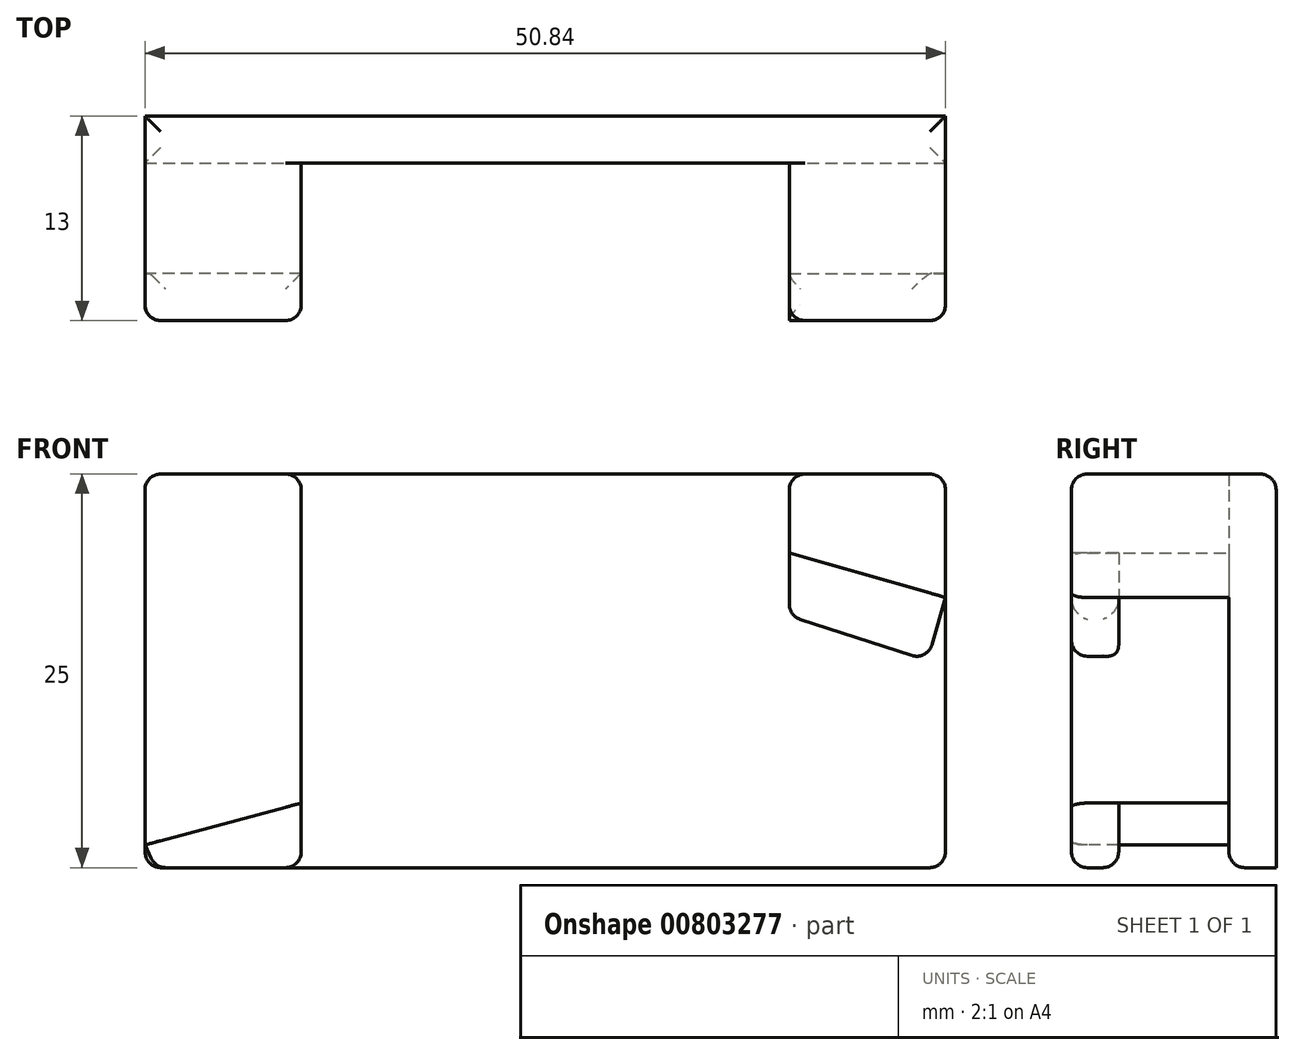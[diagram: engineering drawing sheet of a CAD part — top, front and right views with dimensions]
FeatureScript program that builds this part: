
annotation { "Feature Type Name" : "Feature", "Feature Type Description" : "" }
export const myFeature = defineFeature(function(context is Context, id is Id, definition is map)
    precondition{}
    {
        {
            var Q0;
            Q0=qCreatedBy(makeId("Top.planeOp"),FACE);
            var sketch = newSketch(context, id + "F0", { "sketchPlane" : qUnion([Q0])});
            skPoint(sketch, "E0.rect.middle", {"position": v(0, 0) * mm});
            skLineSegment(sketch, "E1", {"start": v(13.42, 12.71) * mm, "end": v(13.42, 8.71) * mm});
            skLineSegment(sketch, "E2", {"start": v(13.42, 8.7) * mm, "end": v(37.42, 8.71) * mm});
            skLineSegment(sketch, "E3", {"start": v(37.42, 8.71) * mm, "end": v(37.42, 12.71) * mm});
            skLineSegment(sketch, "E4", {"start": v(37.42, 12.71) * mm, "end": v(50.84, 12.71) * mm});
            skLineSegment(sketch, "E5", {"start": v(13.42, 12.71) * mm, "end": v(0, 12.71) * mm});
            skLineSegment(sketch, "E6", {"start": v(0, 0) * mm, "end": v(50.84, 0) * mm});
            skLineSegment(sketch, "E7", {"start": v(0, 12.71) * mm, "end": v(0, 0) * mm});
            skLineSegment(sketch, "E8", {"start": v(50.84, 12.71) * mm, "end": v(50.84, 0) * mm});
            skSolve(sketch);
        }
        {
            var Q0;
            Q0=makeQuery(id+"F0.imprint","IMPRINT",FACE,{"disambiguationData":[TD([[makeQuery(id+"F0.imprint","IMPRINT",EDGE,{"derivedFrom":sQuery(id+"F0.wireOp",EDGE,"E1")}),-1.0]])]});
            extrude(context, id + "F1", {"entities" : qUnion([Q0]), "depth" : 3 * mm, "offsetDistance" : 25 * mm});
        }
        {
            var Q0;
            Q0=makeQuery(id+"F1.opExtrude","SWEPT_FACE",FACE,{"disambiguationData":[OSD([sQuery(id+"F0.wireOp",EDGE,"E6")])]});
            var sketch = newSketch(context, id + "F2", { "sketchPlane" : qUnion([Q0])});
            skLineSegment(sketch, "E9", {"start": v(50.84, 0) * mm, "end": v(50.84, 25) * mm});
            skLineSegment(sketch, "E10", {"start": v(50.84, 25) * mm, "end": v(0, 25) * mm});
            skLineSegment(sketch, "E11", {"start": v(0, 25) * mm, "end": v(0, 0) * mm});
            skLineSegment(sketch, "E12", {"start": v(0, 0) * mm, "end": v(50.84, 0) * mm});
            skSolve(sketch);
        }
        {
            var Q0;
            Q0=qSketchRegion(id+"F2",true);
            extrude(context, id + "F3", {"entities" : qUnion([Q0]), "operationType" : NewBodyOperationType.ADD, "depth" : 3 * mm});
        }
        {
            var Q0;
            Q0=makeQuery(id+"F3.opExtrude","CAP_FACE",FACE,{"disambiguationData":[OSD([sQuery(id+"F2.wireOp",EDGE,"E9"),sQuery(id+"F2.wireOp",EDGE,"E10"),sQuery(id+"F2.wireOp",EDGE,"E11"),sQuery(id+"F2.wireOp",EDGE,"E12")])],"isStart":false});
            var sketch = newSketch(context, id + "F4", { "sketchPlane" : qUnion([Q0])});
            skLineSegment(sketch, "E13", {"start": v(40.92, 25) * mm, "end": v(40.92, 20) * mm});
            skLineSegment(sketch, "E14", {"start": v(40.92, 20) * mm, "end": v(50.84, 17.16) * mm});
            skLineSegment(sketch, "E15", {"start": v(9.92, 25) * mm, "end": v(9.92, 4.1) * mm});
            skLineSegment(sketch, "E16", {"start": v(9.92, 4.1) * mm, "end": v(0, 1.44) * mm});
            skSolve(sketch);
        }
        {
            var Q0;
            Q0=qSketchRegion(id+"F4",true);
            var Q1;
            {var subQ0=sQuery(id+"F4.wireOp",EDGE,"E15");Q1=makeQuery(id+"F4.imprint","IMPRINT",FACE,{"disambiguationData":[TD([[makeQuery(id+"F4.imprint","IMPRINT",EDGE,{"derivedFrom":subQ0}),-1.0]])]});}
            var Q2;
            {var subQ0=sQuery(id+"F4.wireOp",EDGE,"E13");Q2=makeQuery(id+"F4.imprint","IMPRINT",FACE,{"disambiguationData":[TD([[makeQuery(id+"F4.imprint","IMPRINT",EDGE,{"derivedFrom":subQ0}),1.0]])]});}
            extrude(context, id + "F5", {"entities" : qUnion([Q0, Q1, Q2]), "operationType" : NewBodyOperationType.ADD, "depth" : 10 * mm});
        }
        {
            var Q0;
            Q0=makeQuery(id+"F5.opExtrude","CAP_FACE",FACE,{"disambiguationData":[OSD([sQuery(id+"F2.wireOp",EDGE,"E9"),sQuery(id+"F2.wireOp",EDGE,"E10"),sQuery(id+"F4.wireOp",EDGE,"E13"),sQuery(id+"F4.wireOp",EDGE,"E14")])],"isStart":false});
            var sketch = newSketch(context, id + "F6", { "sketchPlane" : qUnion([Q0])});
            skLineSegment(sketch, "E17", {"start": v(50.84, 17.16) * mm, "end": v(49.7, 13.16) * mm});
            skLineSegment(sketch, "E18", {"start": v(40.92, 20) * mm, "end": v(40.92, 16) * mm});
            skLineSegment(sketch, "E19", {"start": v(40.92, 16) * mm, "end": v(49.7, 13.16) * mm});
            skLineSegment(sketch, "E20", {"start": v(40.92, 16) * mm, "end": v(40.92, 20) * mm});
            skSolve(sketch);
        }
        {
            var Q0;
            Q0=qSketchRegion(id+"F6",true);
            var Q1;
            Q1=makeQuery(id+"F6.imprint","IMPRINT",FACE,{"disambiguationData":[TD([[makeQuery(id+"F6.imprint","IMPRINT",EDGE,{"derivedFrom":sQuery(id+"F6.wireOp",EDGE,"E17")}),-1.0]])]});
            extrude(context, id + "F7", {"entities" : qUnion([Q0, Q1]), "oppositeDirection" : true, "depth" : 3 * mm});
        }
        {
            var Q0;
            Q0=makeQuery(id+"F5.opExtrude","CAP_FACE",FACE,{"disambiguationData":[OSD([sQuery(id+"F2.wireOp",EDGE,"E10"),sQuery(id+"F2.wireOp",EDGE,"E11"),sQuery(id+"F4.wireOp",EDGE,"E15"),sQuery(id+"F4.wireOp",EDGE,"E16")])],"isStart":false});
            var sketch = newSketch(context, id + "F8", { "sketchPlane" : qUnion([Q0])});
            skLineSegment(sketch, "E21", {"start": v(9.92, 4.1) * mm, "end": v(9.92, 0) * mm});
            skLineSegment(sketch, "E22", {"start": v(9.92, 0) * mm, "end": v(0.67, 0) * mm});
            skPoint(sketch, "E22.endSnap0", {"position": v(0.67, 0) * mm});
            skLineSegment(sketch, "E23", {"start": v(0, 1.44) * mm, "end": v(0.67, 0) * mm});
            skSolve(sketch);
        }
        {
            var Q0;
            Q0=qSketchRegion(id+"F8",true);
            var Q1;
            Q1=makeQuery(id+"F8.imprint","IMPRINT",FACE,{"disambiguationData":[TD([[makeQuery(id+"F8.imprint","IMPRINT",EDGE,{"derivedFrom":sQuery(id+"F8.wireOp",EDGE,"E21")}),-1.0]])]});
            extrude(context, id + "F9", {"entities" : qUnion([Q0, Q1]), "oppositeDirection" : true, "depth" : 3 * mm, "offsetDistance" : 25 * mm});
        }
        {
            var Q0;
            Q0=makeQuery(id+"F5.opExtrude","CAP_EDGE",EDGE,{"disambiguationData":[OSD([sQuery(id+"F4.wireOp",EDGE,"E15")])],"isStart":true});
            var Q1;
            Q1=makeQuery(id+"F5.opExtrude","CAP_EDGE",EDGE,{"disambiguationData":[OSD([sQuery(id+"F4.wireOp",EDGE,"E14")])],"isStart":true});
            var Q2;
            Q2=makeQuery(id+"F5.opExtrude","CAP_EDGE",EDGE,{"disambiguationData":[OSD([sQuery(id+"F4.wireOp",EDGE,"E16")])],"isStart":true});
            var Q3;
            Q3=makeQuery(id+"F1.opExtrude","CAP_EDGE",EDGE,{"disambiguationData":[OSD([sQuery(id+"F0.wireOp",EDGE,"E6")])],"isStart":false});
            var Q4;
            Q4=makeQuery(id+"F1.opExtrude","SWEPT_EDGE",EDGE,{"disambiguationData":[OSD([sQuery(id+"F0.wireOp",EDGE,"E1"),sQuery(id+"F0.wireOp",EDGE,"E2")])]});
            fillet(context, id + "F10", {"entities" : qUnion([Q0, Q1, Q2, Q3, Q4]), "radius" : .5 * mm, "tangentPropagation" : true, "allowEdgeOverflow" : false});
        }
        {
            var Q0;
            Q0=makeQuery(id+"F3.boolean.opBoolean","MERGE",FACE,{"derivedFrom":[makeQuery(id+"F1.opExtrude","CAP_FACE",FACE,{"disambiguationData":[OSD([sQuery(id+"F0.wireOp",EDGE,"E1"),sQuery(id+"F0.wireOp",EDGE,"E2"),sQuery(id+"F0.wireOp",EDGE,"E3"),sQuery(id+"F0.wireOp",EDGE,"E4"),sQuery(id+"F0.wireOp",EDGE,"E5"),sQuery(id+"F0.wireOp",EDGE,"E6"),sQuery(id+"F0.wireOp",EDGE,"E7"),sQuery(id+"F0.wireOp",EDGE,"E8")])],"isStart":true}),makeQuery(id+"F3.opExtrude","SWEPT_FACE",FACE,{"disambiguationData":[OSD([sQuery(id+"F2.wireOp",EDGE,"E12")])]})]});
            var sketch = newSketch(context, id + "F11", { "sketchPlane" : qUnion([Q0])});
            skPoint(sketch, "E24.orphan", {"position": v(38.32, -23.71) * mm});
            skLineSegment(sketch, "E25", {"start": v(37.42, -12.71) * mm, "end": v(37.42, -8.71) * mm});
            skLineSegment(sketch, "E26", {"start": v(37.42, -8.71) * mm, "end": v(13.42, -8.71) * mm});
            skLineSegment(sketch, "E27", {"start": v(13.42, -8.71) * mm, "end": v(13.42, -12.71) * mm});
            skLineSegment(sketch, "E28", {"start": v(0, -23.71) * mm, "end": v(0, -12.71) * mm});
            skLineSegment(sketch, "E29", {"start": v(30, -23.71) * mm, "end": v(30, -12.71) * mm});
            skLineSegment(sketch, "E30", {"start": v(30, -12.71) * mm, "end": v(37.42, -12.71) * mm});
            skLineSegment(sketch, "E31", {"start": v(13.42, -12.71) * mm, "end": v(0, -12.71) * mm});
            skLineSegment(sketch, "E32", {"start": v(0, -23.71) * mm, "end": v(30, -23.71) * mm});
            skSolve(sketch);
        }
        {
            var Q0;
            Q0=makeQuery(id+"F11.imprint","IMPRINT",FACE,{"disambiguationData":[TD([[makeQuery(id+"F11.imprint","IMPRINT",EDGE,{"derivedFrom":sQuery(id+"F11.wireOp",EDGE,"E28")}),-1.0]])]});
            extrude(context, id + "F12", {"entities" : qUnion([Q0]), "operationType" : NewBodyOperationType.ADD, "oppositeDirection" : true, "depth" : 3 * mm, "offsetDistance" : 25 * mm});
        }
        {
            var Q0;
            Q0=makeQuery(id+"F3.opExtrude","CAP_EDGE",EDGE,{"disambiguationData":[OSD([sQuery(id+"F2.wireOp",EDGE,"E12")])],"isStart":false});
            var Q1;
            Q1=makeQuery(id+"F3.boolean.opBoolean","MERGE",EDGE,{"derivedFrom":[makeQuery(id+"F1.opExtrude","CAP_EDGE",EDGE,{"disambiguationData":[OSD([sQuery(id+"F0.wireOp",EDGE,"E7")])],"isStart":true}),makeQuery(id+"F3.opExtrude","SWEPT_EDGE",EDGE,{"disambiguationData":[OSD([sQuery(id+"F2.wireOp",EDGE,"E11"),sQuery(id+"F2.wireOp",EDGE,"E12")])]})]});
            var Q2;
            Q2=makeQuery(id+"F3.boolean.opBoolean","MERGE",EDGE,{"derivedFrom":[makeQuery(id+"F1.opExtrude","CAP_EDGE",EDGE,{"disambiguationData":[OSD([sQuery(id+"F0.wireOp",EDGE,"E8")])],"isStart":true}),makeQuery(id+"F3.opExtrude","SWEPT_EDGE",EDGE,{"disambiguationData":[OSD([sQuery(id+"F2.wireOp",EDGE,"E9"),sQuery(id+"F2.wireOp",EDGE,"E12")])]})]});
            var Q3;
            Q3=makeQuery(id+"F5.opExtrude","CAP_EDGE",EDGE,{"disambiguationData":[OSD([sQuery(id+"F4.wireOp",EDGE,"E15")])],"isStart":false});
            var Q4;
            Q4=makeQuery(id+"F5.opExtrude","CAP_EDGE",EDGE,{"disambiguationData":[OSD([sQuery(id+"F2.wireOp",EDGE,"E11")])],"isStart":false});
            var Q5;
            Q5=makeQuery(id+"F3.opExtrude","CAP_EDGE",EDGE,{"disambiguationData":[OSD([sQuery(id+"F2.wireOp",EDGE,"E10")])],"isStart":true});
            var Q6;
            {var subQ0=sQuery(id+"F2.wireOp",EDGE,"E10");var subQ1=makeQuery(id+"F3.opExtrude","CAP_EDGE",EDGE,{"disambiguationData":[OSD([subQ0])],"isStart":false});Q6=makeQuery(id+"F5.opExtrude","CAP_EDGE",EDGE,{"disambiguationData":[OSD([subQ0]),TDD([makeQuery(id+"F4.imprint","IMPRINT",EDGE,{"disambiguationData":[TD([[makeQuery(id+"F4.imprint","INTERSECT",VERTEX,{"derivedFrom":[subQ1,makeQuery(id+"F3.opExtrude","CAP_EDGE",EDGE,{"disambiguationData":[OSD([sQuery(id+"F2.wireOp",EDGE,"E11")])],"isStart":false})]}),1.0]])],"derivedFrom":subQ1})])],"isStart":false});}
            var Q7;
            {var subQ0=sQuery(id+"F2.wireOp",EDGE,"E11");var subQ1=sQuery(id+"F2.wireOp",EDGE,"E10");Q7=makeQuery(id+"F5.boolean.opBoolean","MERGE",EDGE,{"derivedFrom":[makeQuery(id+"F3.opExtrude","SWEPT_EDGE",EDGE,{"disambiguationData":[OSD([subQ1,subQ0])]}),makeQuery(id+"F5.opExtrude","SWEPT_EDGE",EDGE,{"disambiguationData":[OSD([subQ1,subQ0])]})]});}
            var Q8;
            Q8=makeQuery(id+"F5.opExtrude","SWEPT_EDGE",EDGE,{"disambiguationData":[OSD([sQuery(id+"F2.wireOp",EDGE,"E10"),sQuery(id+"F4.wireOp",EDGE,"E15")])]});
            var Q9;
            Q9=makeQuery(id+"F5.opExtrude","SWEPT_EDGE",EDGE,{"disambiguationData":[OSD([sQuery(id+"F2.wireOp",EDGE,"E10"),sQuery(id+"F4.wireOp",EDGE,"E13")])]});
            var Q10;
            {var subQ0=sQuery(id+"F2.wireOp",EDGE,"E10");var subQ1=makeQuery(id+"F3.opExtrude","CAP_EDGE",EDGE,{"disambiguationData":[OSD([subQ0])],"isStart":false});Q10=makeQuery(id+"F5.opExtrude","CAP_EDGE",EDGE,{"disambiguationData":[OSD([subQ0]),TDD([makeQuery(id+"F4.imprint","IMPRINT",EDGE,{"disambiguationData":[TD([[makeQuery(id+"F4.imprint","INTERSECT",VERTEX,{"derivedFrom":[makeQuery(id+"F3.opExtrude","CAP_EDGE",EDGE,{"disambiguationData":[OSD([sQuery(id+"F2.wireOp",EDGE,"E9")])],"isStart":false}),subQ1]}),-1.0]])],"derivedFrom":subQ1})])],"isStart":false});}
            var Q11;
            {var subQ0=sQuery(id+"F2.wireOp",EDGE,"E10");var subQ1=sQuery(id+"F2.wireOp",EDGE,"E9");Q11=makeQuery(id+"F5.boolean.opBoolean","MERGE",EDGE,{"derivedFrom":[makeQuery(id+"F3.opExtrude","SWEPT_EDGE",EDGE,{"disambiguationData":[OSD([subQ1,subQ0])]}),makeQuery(id+"F5.opExtrude","SWEPT_EDGE",EDGE,{"disambiguationData":[OSD([subQ1,subQ0])]})]});}
            var Q12;
            Q12=makeQuery(id+"F5.opExtrude","CAP_EDGE",EDGE,{"disambiguationData":[OSD([sQuery(id+"F4.wireOp",EDGE,"E13")])],"isStart":false});
            var Q13;
            Q13=makeQuery(id+"F7.opExtrude","CAP_EDGE",EDGE,{"disambiguationData":[OSD([sQuery(id+"F6.wireOp",EDGE,"E20")])],"isStart":true});
            var Q14;
            Q14=makeQuery(id+"F7.opExtrude","CAP_EDGE",EDGE,{"disambiguationData":[OSD([sQuery(id+"F6.wireOp",EDGE,"E17")])],"isStart":true});
            var Q15;
            Q15=makeQuery(id+"F5.opExtrude","CAP_EDGE",EDGE,{"disambiguationData":[OSD([sQuery(id+"F2.wireOp",EDGE,"E9")])],"isStart":false});
            var Q16;
            Q16=makeQuery(id+"F9.opExtrude","CAP_EDGE",EDGE,{"disambiguationData":[OSD([sQuery(id+"F8.wireOp",EDGE,"E21")])],"isStart":true});
            var Q17;
            Q17=makeQuery(id+"F9.opExtrude","CAP_EDGE",EDGE,{"disambiguationData":[OSD([sQuery(id+"F8.wireOp",EDGE,"E23")])],"isStart":true});
            var Q18;
            Q18=makeQuery(id+"F7.opExtrude","CAP_EDGE",EDGE,{"disambiguationData":[OSD([sQuery(id+"F6.wireOp",EDGE,"E19")])],"isStart":false});
            var Q19;
            Q19=makeQuery(id+"F9.opExtrude","CAP_EDGE",EDGE,{"disambiguationData":[OSD([sQuery(id+"F8.wireOp",EDGE,"E22")])],"isStart":false});
            var Q20;
            Q20=makeQuery(id+"F9.opExtrude","SWEPT_EDGE",EDGE,{"disambiguationData":[OSD([sQuery(id+"F8.wireOp",EDGE,"E21"),sQuery(id+"F8.wireOp",EDGE,"E22")])]});
            var Q21;
            Q21=makeQuery(id+"F9.opExtrude","SWEPT_EDGE",EDGE,{"disambiguationData":[OSD([sQuery(id+"F8.wireOp",EDGE,"E22"),sQuery(id+"F8.wireOp",EDGE,"E23")])]});
            var Q22;
            Q22=makeQuery(id+"F7.opExtrude","SWEPT_EDGE",EDGE,{"disambiguationData":[OSD([sQuery(id+"F6.wireOp",EDGE,"E17"),sQuery(id+"F6.wireOp",EDGE,"E19")])]});
            var Q23;
            Q23=makeQuery(id+"F7.opExtrude","SWEPT_EDGE",EDGE,{"disambiguationData":[OSD([sQuery(id+"F6.wireOp",EDGE,"E19"),sQuery(id+"F6.wireOp",EDGE,"E20")])]});
            var Q24;
            Q24=makeQuery(id+"F7.opExtrude","CAP_EDGE",EDGE,{"disambiguationData":[OSD([sQuery(id+"F6.wireOp",EDGE,"E19")])],"isStart":true});
            var Q25;
            Q25=makeQuery(id+"F9.opExtrude","CAP_EDGE",EDGE,{"disambiguationData":[OSD([sQuery(id+"F8.wireOp",EDGE,"E22")])],"isStart":true});
            fillet(context, id + "F13", {"entities" : qUnion([Q0, Q1, Q2, Q3, Q4, Q5, Q6, Q7, Q8, Q9, Q10, Q11, Q12, Q13, Q14, Q15, Q16, Q17, Q18, Q19, Q20, Q21, Q22, Q23, Q24, Q25]), "radius" : 1 * mm, "tangentPropagation" : true, "allowEdgeOverflow" : false});
        }
        {
            var Q0;
            {var subQ0=sQuery(id+"F0.wireOp",EDGE,"E8");var subQ1=sQuery(id+"F0.wireOp",EDGE,"E7");var subQ2=sQuery(id+"F0.wireOp",EDGE,"E6");var subQ3=sQuery(id+"F0.wireOp",EDGE,"E5");var subQ4=sQuery(id+"F0.wireOp",EDGE,"E4");var subQ5=sQuery(id+"F0.wireOp",EDGE,"E3");var subQ6=sQuery(id+"F0.wireOp",EDGE,"E2");var subQ7=sQuery(id+"F0.wireOp",EDGE,"E1");Q0=makeQuery(id+"F12.boolean.opBoolean","MERGE",FACE,{"derivedFrom":[makeQuery(id+"F1.opExtrude","CAP_FACE",FACE,{"disambiguationData":[OSD([subQ7,subQ6,subQ5,subQ4,subQ3,subQ2,subQ1,subQ0])],"isStart":false}),makeQuery(id+"F12.opExtrude","CAP_FACE",FACE,{"disambiguationData":[OSD([subQ7,subQ6,subQ5,subQ4,subQ3,subQ2,subQ1,subQ0,sQuery(id+"F2.wireOp",EDGE,"E12"),sQuery(id+"F11.wireOp",EDGE,"8vjeRnlP-fWbf-NYoU-CAz4-IPFx9vDDlTFN"),sQuery(id+"F11.wireOp",EDGE,"LpTD77hC-0NfJ-vC53-LtAF-cYjLVDu7FIAZ"),sQuery(id+"F11.wireOp",EDGE,"NnwKIxEU-GQhr-w3og-xfwb-NFp2FZGWKe5B"),sQuery(id+"F11.wireOp",EDGE,"E25"),sQuery(id+"F11.wireOp",EDGE,"E26"),sQuery(id+"F11.wireOp",EDGE,"E27")])],"isStart":false})]});}
            var sketch = newSketch(context, id + "F14", { "sketchPlane" : qUnion([Q0])});
            skCircle(sketch, "E33", {"center": v(15.42, 13.5) * mm, "radius": 1.6 * mm});
            skPoint(sketch, "E34.orphan", {"position": v(25.42, 23.71) * mm});
            skPoint(sketch, "E35.orphan", {"position": v(25.42, 0.5) * mm});
            skSolve(sketch);
        }
        {
            var Q0;
            Q0=makeQuery(id+"F14.imprint","IMPRINT",FACE,{"disambiguationData":[TD([[makeQuery(id+"F14.imprint","IMPRINT",EDGE,{"derivedFrom":sQuery(id+"F14.wireOp",EDGE,"E33")}),1.0]])]});
            extrude(context, id + "F15", {"entities" : qUnion([Q0]), "operationType" : NewBodyOperationType.REMOVE, "oppositeDirection" : true, "depth" : 25 * mm, "offsetDistance" : 25 * mm});
        }
        {
            var Q0;
            {var subQ0=sQuery(id+"F2.wireOp",EDGE,"E9");Q0=makeQuery(id+"F5.boolean.opBoolean","MERGE",FACE,{"derivedFrom":[makeQuery(id+"F3.boolean.opBoolean","MERGE",FACE,{"derivedFrom":[makeQuery(id+"F1.opExtrude","SWEPT_FACE",FACE,{"disambiguationData":[OSD([sQuery(id+"F0.wireOp",EDGE,"E8")])]}),makeQuery(id+"F3.opExtrude","SWEPT_FACE",FACE,{"disambiguationData":[OSD([subQ0])]})]}),makeQuery(id+"F5.opExtrude","SWEPT_FACE",FACE,{"disambiguationData":[OSD([subQ0])]})]});}
            var sketch = newSketch(context, id + "F16", { "sketchPlane" : qUnion([Q0])});
            skLineSegment(sketch, "E36.bottom", {"start": v(0, 5.8) * mm, "end": v(25.47, 5.8) * mm});
            skLineSegment(sketch, "E36.top", {"start": v(0, -2.2) * mm, "end": v(25.47, -2.2) * mm});
            skLineSegment(sketch, "E36.left", {"start": v(0, 5.8) * mm, "end": v(0, -2.2) * mm});
            skLineSegment(sketch, "E36.right", {"start": v(25.47, 5.8) * mm, "end": v(25.47, -2.2) * mm});
            skSolve(sketch);
        }
        {
            var Q0;
            {var subQ8=sQuery(id+"F16.wireOp",EDGE,"E36.bottom");Q0=makeQuery(id+"F16.imprint","IMPRINT",FACE,{"disambiguationData":[TD([[makeQuery(id+"F16.imprint","IMPRINT",EDGE,{"derivedFrom":subQ8}),-1.0]])]});}
            var Q1;
            {var subQ1=sQuery(id+"F0.wireOp",EDGE,"E8");Q1=makeQuery(id+"F16.imprint","IMPRINT",FACE,{"disambiguationData":[TD([[makeQuery(id+"F16.imprint","IMPRINT",EDGE,{"derivedFrom":makeQuery(id+"F1.opExtrude","CAP_EDGE",EDGE,{"disambiguationData":[OSD([subQ1])],"isStart":false})}),1.0]])]});}
            extrude(context, id + "F17", {"entities" : qUnion([Q0, Q1]), "operationType" : NewBodyOperationType.REMOVE, "oppositeDirection" : true, "depth" : 59.7 * mm, "offsetDistance" : 25 * mm});
        }
    });
